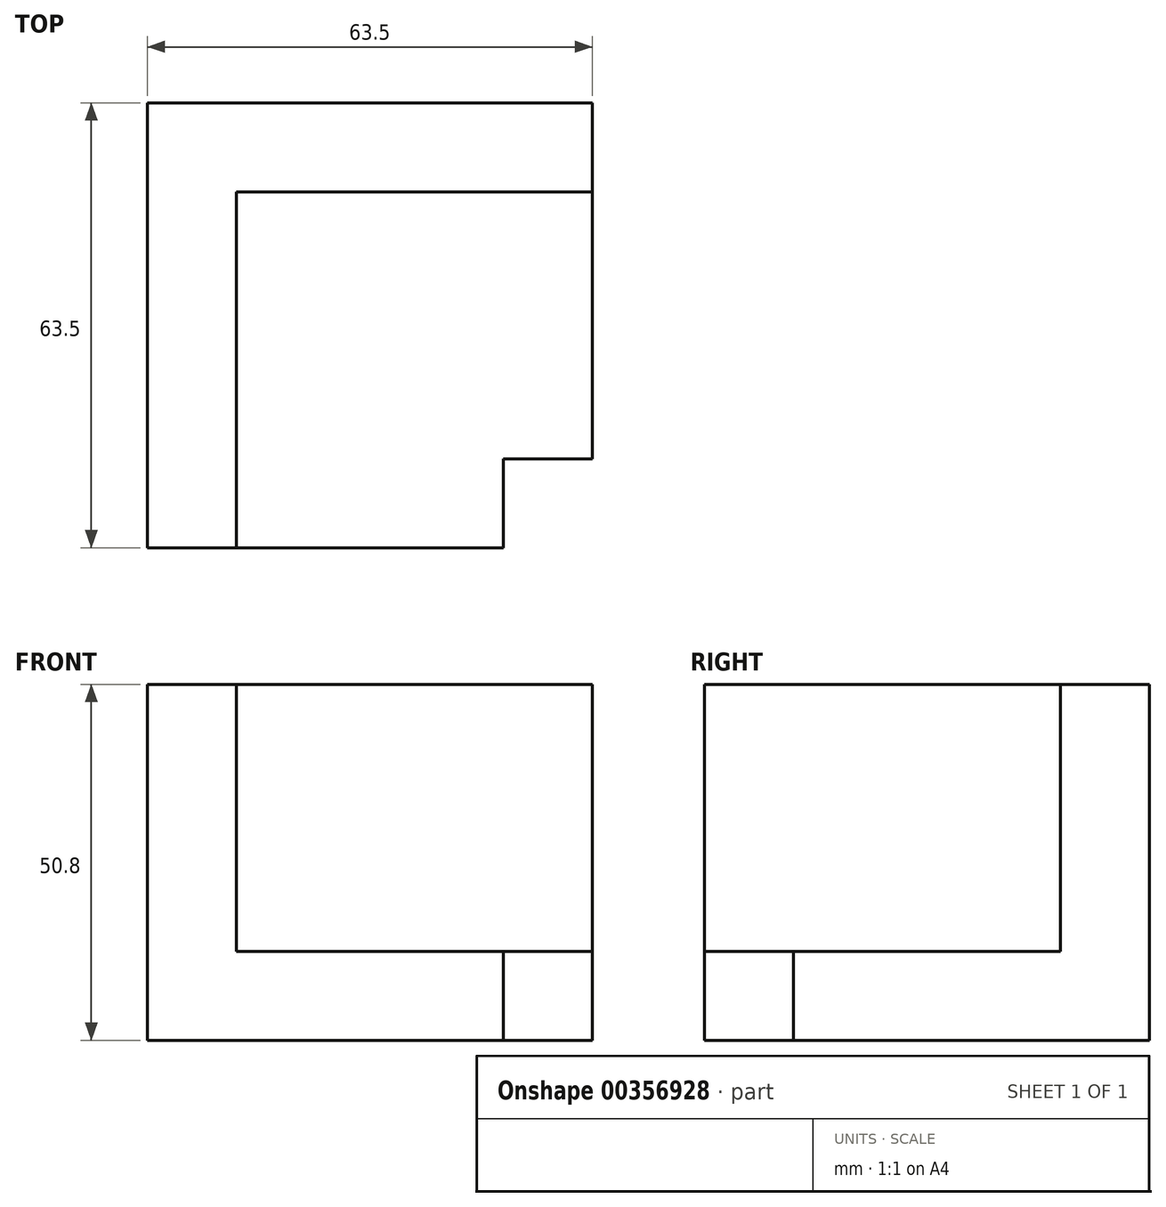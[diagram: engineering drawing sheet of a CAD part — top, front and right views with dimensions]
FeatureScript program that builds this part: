
annotation { "Feature Type Name" : "Feature", "Feature Type Description" : "" }
export const myFeature = defineFeature(function(context is Context, id is Id, definition is map)
    precondition{}
    {
        {
            var Q0;
            Q0=qCreatedBy(makeId("Front.planeOp"),FACE);
            var sketch = newSketch(context, id + "F0", { "sketchPlane" : qUnion([Q0])});
            skLineSegment(sketch, "E0.bottom", {"start": v(0, 0) * mm, "end": v(12.7, 0) * mm});
            skLineSegment(sketch, "E0.top", {"start": v(0, -50.8) * mm, "end": v(12.7, -50.8) * mm});
            skLineSegment(sketch, "E0.left", {"start": v(0, 0) * mm, "end": v(0, -50.8) * mm});
            skLineSegment(sketch, "E0.right", {"start": v(12.7, 0) * mm, "end": v(12.7, -50.8) * mm});
            skSolve(sketch);
        }
        {
            var Q0;
            Q0 = qSketchRegion(id + "F0", true);
            var Q1;
            Q1=makeQuery(id+"F0.imprint","IMPRINT",FACE,{"disambiguationData":[TD([[makeQuery(id+"F0.imprint","IMPRINT",EDGE,{"derivedFrom":sQuery(id+"F0.wireOp",EDGE,"E0.bottom")}),-1.0]])]});
            extrude(context, id + "F1", {"entities" : qUnion([Q0, Q1]), "depth" : 63.5 * mm});
        }
        {
            var Q0;
            Q0=makeQuery(id+"F1.opExtrude","SWEPT_FACE",FACE,{"disambiguationData":[OSD([sQuery(id+"F0.wireOp",EDGE,"E0.right")])]});
            var sketch = newSketch(context, id + "F2", { "sketchPlane" : qUnion([Q0])});
            skLineSegment(sketch, "E1.bottom", {"start": v(0, -50.8) * mm, "end": v(-12.7, -50.8) * mm});
            skLineSegment(sketch, "E1.top", {"start": v(0, 0) * mm, "end": v(-12.7, 0) * mm});
            skLineSegment(sketch, "E1.left", {"start": v(0, -50.8) * mm, "end": v(0, 0) * mm});
            skLineSegment(sketch, "E1.right", {"start": v(-12.7, -50.8) * mm, "end": v(-12.7, 0) * mm});
            skSolve(sketch);
        }
        {
            var Q0;
            Q0 = qSketchRegion(id + "F2", true);
            extrude(context, id + "F3", {"entities" : qUnion([Q0]), "operationType" : NewBodyOperationType.ADD, "depth" : 50.8 * mm});
        }
        {
            var Q0;
            Q0=makeQuery(id+"F1.opExtrude","SWEPT_FACE",FACE,{"disambiguationData":[OSD([sQuery(id+"F0.wireOp",EDGE,"E0.right")])]});
            var sketch = newSketch(context, id + "F4", { "sketchPlane" : qUnion([Q0])});
            skLineSegment(sketch, "E2.bottom", {"start": v(-63.5, -50.8) * mm, "end": v(-12.7, -50.8) * mm});
            skLineSegment(sketch, "E2.top", {"start": v(-63.5, -38.1) * mm, "end": v(-12.7, -38.1) * mm});
            skLineSegment(sketch, "E2.left", {"start": v(-63.5, -50.8) * mm, "end": v(-63.5, -38.1) * mm});
            skLineSegment(sketch, "E2.right", {"start": v(-12.7, -50.8) * mm, "end": v(-12.7, -38.1) * mm});
            skSolve(sketch);
        }
        {
            var Q0;
            Q0 = qSketchRegion(id + "F4", true);
            extrude(context, id + "F5", {"entities" : qUnion([Q0]), "operationType" : NewBodyOperationType.ADD, "depth" : 50.8 * mm});
        }
        {
            var Q0;
            Q0=makeQuery(id+"F5.boolean.opBoolean","MERGE",FACE,{"derivedFrom":[makeQuery(id+"F1.opExtrude","CAP_FACE",FACE,{"disambiguationData":[OSD([sQuery(id+"F0.wireOp",EDGE,"E0.bottom"),sQuery(id+"F0.wireOp",EDGE,"E0.top"),sQuery(id+"F0.wireOp",EDGE,"E0.left"),sQuery(id+"F0.wireOp",EDGE,"E0.right")])],"isStart":false}),makeQuery(id+"F5.opExtrude","SWEPT_FACE",FACE,{"disambiguationData":[OSD([sQuery(id+"F4.wireOp",EDGE,"E2.left")])]})]});
            var sketch = newSketch(context, id + "F6", { "sketchPlane" : qUnion([Q0])});
            skLineSegment(sketch, "E3.bottom", {"start": v(63.5, -50.8) * mm, "end": v(50.8, -50.8) * mm});
            skLineSegment(sketch, "E3.top", {"start": v(63.5, -38.1) * mm, "end": v(50.8, -38.1) * mm});
            skLineSegment(sketch, "E3.left", {"start": v(63.5, -50.8) * mm, "end": v(63.5, -38.1) * mm});
            skLineSegment(sketch, "E3.right", {"start": v(50.8, -50.8) * mm, "end": v(50.8, -38.1) * mm});
            skSolve(sketch);
        }
        {
            var Q0;
            Q0 = qSketchRegion(id + "F6", true);
            extrude(context, id + "F7", {"entities" : qUnion([Q0]), "operationType" : NewBodyOperationType.REMOVE, "oppositeDirection" : true, "depth" : 12.7 * mm});
        }
    });
